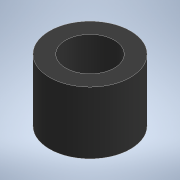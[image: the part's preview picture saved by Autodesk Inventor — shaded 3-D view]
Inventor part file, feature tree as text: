
AUTODESK INVENTOR PART (.ipt)
format: ipt  version: 2022.2 (Build 262287010, 287A)  size: 95,232 bytes
history: native  units: mm
features: extrude x1, sketch x1
ambient origin geometry x8: Origin, YZ Plane, XZ Plane, XY Plane, X Axis, Y Axis, Z Axis, Center Point
bodies: Volumenkörper1 (feature_tree)
feature tree (2):
  extrude  "Extrusion1"  Depth=7.7mm
  sketch  "Skizze1"  dims[d0=6.0mm d1=2.0mm d2=7.7mm d3=0.0mm]
